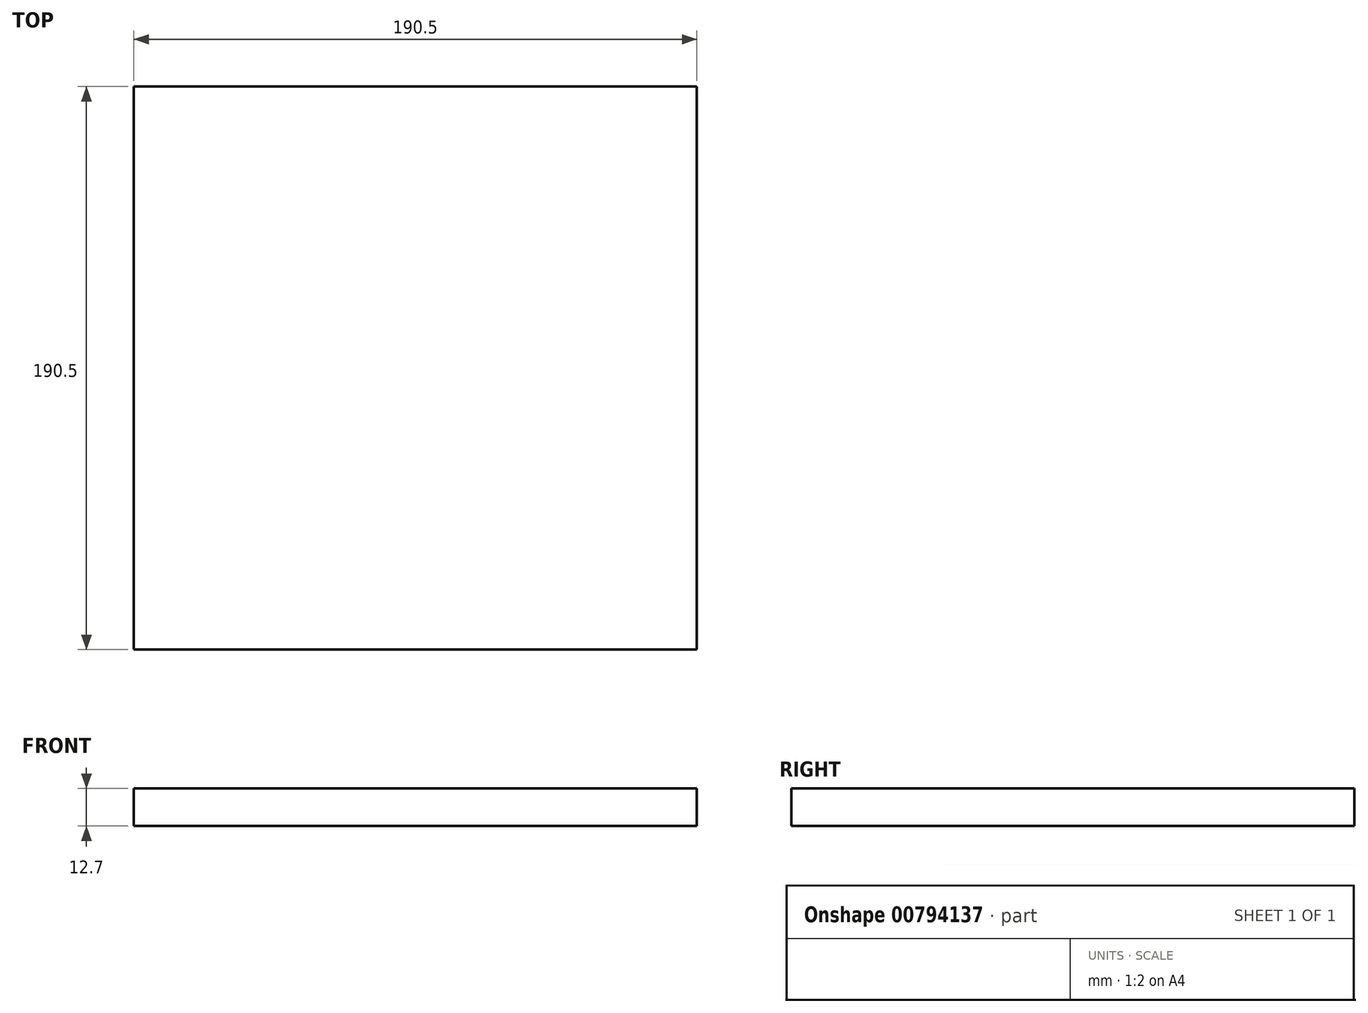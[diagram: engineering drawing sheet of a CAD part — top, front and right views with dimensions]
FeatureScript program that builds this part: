
annotation { "Feature Type Name" : "Feature", "Feature Type Description" : "" }
export const myFeature = defineFeature(function(context is Context, id is Id, definition is map)
    precondition{}
    {
        {
            var Q0;
            Q0=qCreatedBy(makeId("Top.planeOp"),FACE);
            var sketch = newSketch(context, id + "F0", { "sketchPlane" : qUnion([Q0])});
            skLineSegment(sketch, "E0.bottom", {"start": v(95.25, 95.25) * mm, "end": v(-95.25, 95.25) * mm});
            skLineSegment(sketch, "E0.top", {"start": v(95.25, -95.25) * mm, "end": v(-95.25, -95.25) * mm});
            skLineSegment(sketch, "E0.left", {"start": v(95.25, 95.25) * mm, "end": v(95.25, -95.25) * mm});
            skLineSegment(sketch, "E0.right", {"start": v(-95.25, 95.25) * mm, "end": v(-95.25, -95.25) * mm});
            skPoint(sketch, "E0.middle", {"position": v(0, 0) * mm});
            skSolve(sketch);
        }
        {
            var Q0;
            Q0=makeQuery(id+"F0.imprint","IMPRINT",FACE,{"disambiguationData":[TD([[makeQuery(id+"F0.imprint","IMPRINT",EDGE,{"derivedFrom":sQuery(id+"F0.wireOp",EDGE,"E0.bottom")}),1.0]])]});
            extrude(context, id + "F1", {"entities" : qUnion([Q0]), "depth" : 12.7 * mm, "offsetDistance" : 25.4 * mm});
        }
    });
